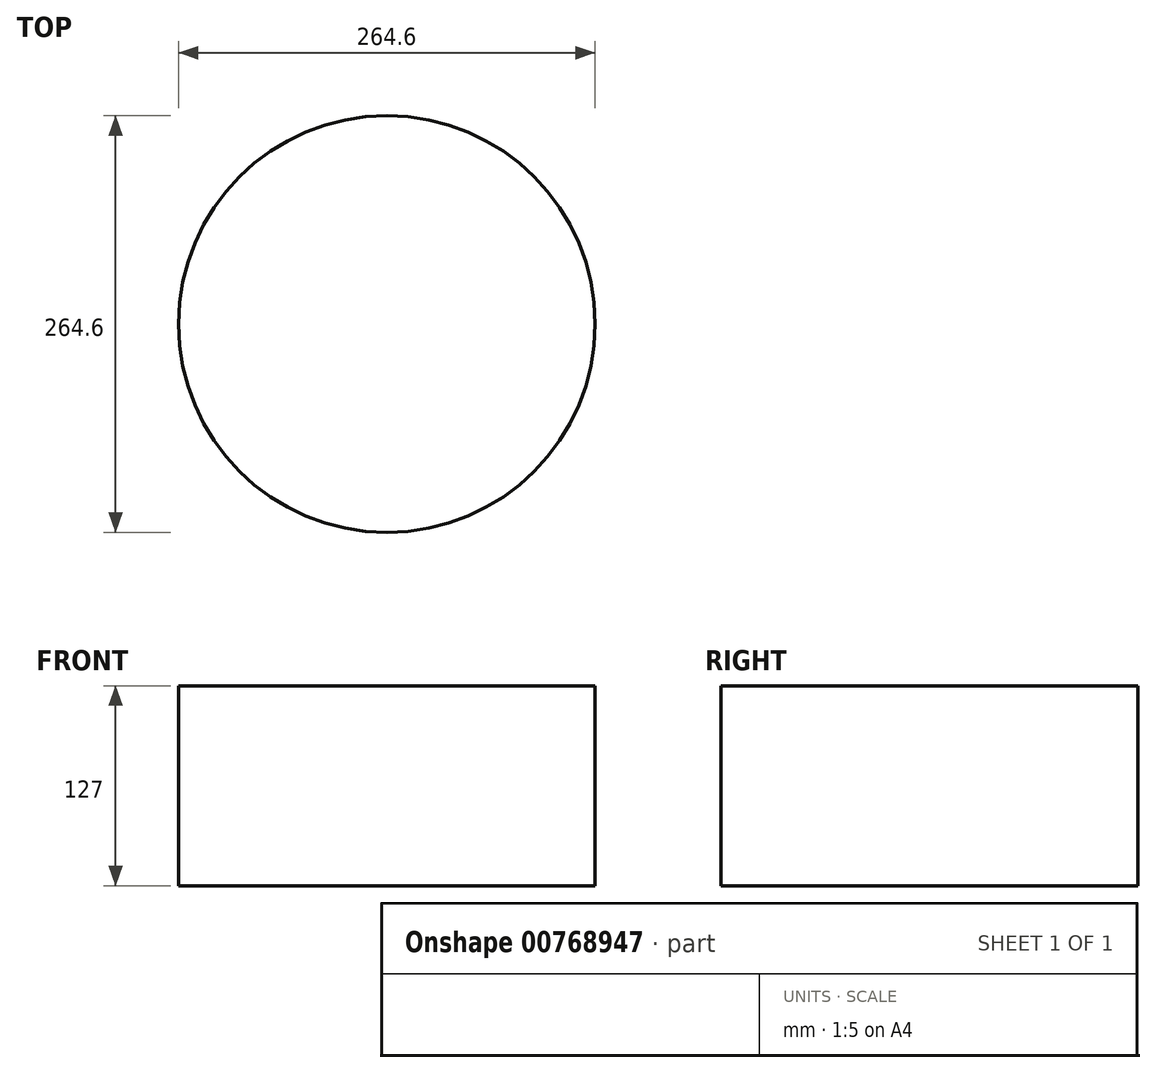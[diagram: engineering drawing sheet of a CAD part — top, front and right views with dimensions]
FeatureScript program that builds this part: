
annotation { "Feature Type Name" : "Feature", "Feature Type Description" : "" }
export const myFeature = defineFeature(function(context is Context, id is Id, definition is map)
    precondition{}
    {
        {
            var Q0;
            Q0=qCreatedBy(makeId("Top.planeOp"),FACE);
            var sketch = newSketch(context, id + "F0", { "sketchPlane" : qUnion([Q0])});
            skCircle(sketch, "E0", {"center": v(0, 0) * mm, "radius": 132.3 * mm});
            skSolve(sketch);
        }
        {
            var Q0;
            Q0=makeQuery(id+"F0.imprint","IMPRINT",FACE,{"disambiguationData":[TD([[makeQuery(id+"F0.imprint","IMPRINT",EDGE,{"derivedFrom":sQuery(id+"F0.wireOp",EDGE,"E0")}),1.0]])]});
            extrude(context, id + "F1", {"entities" : qUnion([Q0]), "endBound" : BoundingType.SYMMETRIC, "depth" : 127 * mm, "offsetDistance" : 25.4 * mm});
        }
    });
